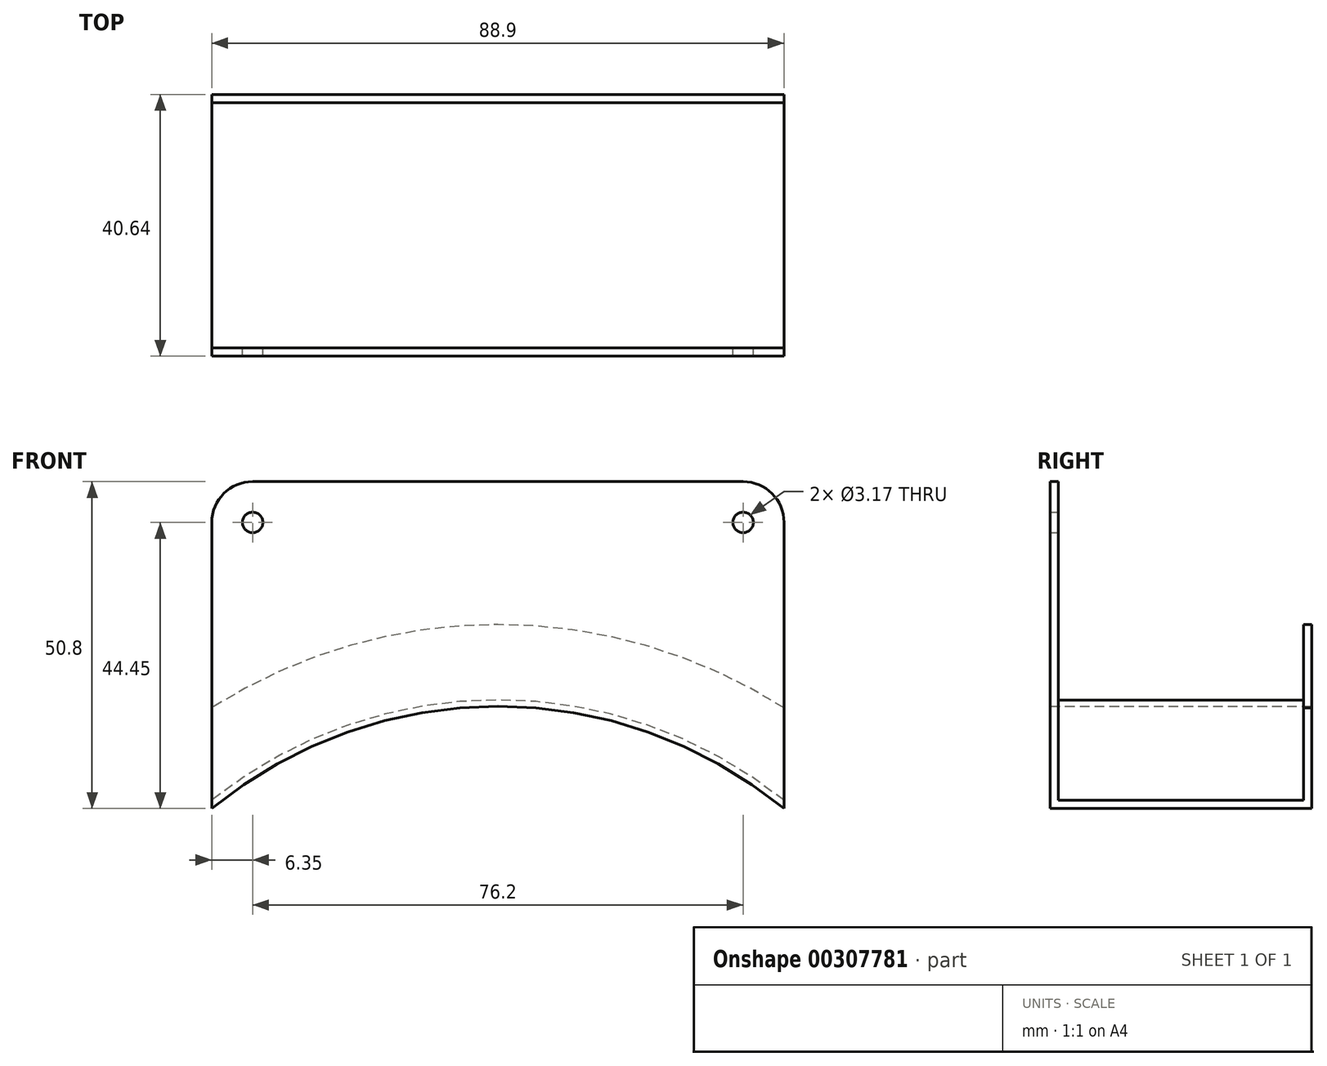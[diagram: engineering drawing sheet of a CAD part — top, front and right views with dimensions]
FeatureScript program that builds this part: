
annotation { "Feature Type Name" : "Feature", "Feature Type Description" : "" }
export const myFeature = defineFeature(function(context is Context, id is Id, definition is map)
    precondition{}
    {
        {
            var Q0;
            Q0=qCreatedBy(makeId("Front.planeOp"),FACE);
            var sketch = newSketch(context, id + "F0", { "sketchPlane" : qUnion([Q0])});
            skLineSegment(sketch, "E0", {"start": v(-44.45, 0) * mm, "end": v(44.45, 0) * mm});
            skArc(sketch, "E1", {"start": v(44.45, 0) * mm, "mid": v(0, 15.88) * mm, "end": v(-44.45, 0) * mm});
            skPoint(sketch, "E2", {"position": v(0, 15.88) * mm});
            skPoint(sketch, "E3", {"position": v(0, 28.58) * mm});
            skArc(sketch, "E4", {"start": v(44.45, 15.64) * mm, "mid": v(0, 28.58) * mm, "end": v(-44.45, 15.64) * mm});
            skLineSegment(sketch, "E5", {"start": v(-44.45, 15.64) * mm, "end": v(-44.45, 0) * mm});
            skLineSegment(sketch, "E6", {"start": v(44.45, 15.64) * mm, "end": v(44.45, 0) * mm});
            skSolve(sketch);
        }
        {
            var Q0;
            Q0=makeQuery(id+"F0.imprint","IMPRINT",FACE,{"disambiguationData":[TD([[makeQuery(id+"F0.imprint","IMPRINT",EDGE,{"derivedFrom":sQuery(id+"F0.wireOp",EDGE,"E1")}),-1.0]])]});
            extrude(context, id + "F1", {"entities" : qUnion([Q0]), "depth" : 1.27 * mm});
        }
        {
            var Q0;
            Q0=makeQuery(id+"F1.opExtrude","CAP_FACE",FACE,{"disambiguationData":[OSD([sQuery(id+"F0.wireOp",EDGE,"E1"),sQuery(id+"F0.wireOp",EDGE,"E4"),sQuery(id+"F0.wireOp",EDGE,"E5"),sQuery(id+"F0.wireOp",EDGE,"E6")])],"isStart":false});
            var sketch = newSketch(context, id + "F2", { "sketchPlane" : qUnion([Q0])});
            skArc(sketch, "E7", {"start": v(44.45, 0) * mm, "mid": v(0, 15.88) * mm, "end": v(-44.45, 0) * mm});
            skArc(sketch, "E8", {"start": v(44.45, 1.27) * mm, "mid": v(0, 16.86) * mm, "end": v(-44.45, 1.27) * mm});
            skLineSegment(sketch, "E9", {"start": v(44.45, 1.27) * mm, "end": v(44.45, 0) * mm});
            skSolve(sketch);
        }
        {
            var Q0;
            {var subQ0=sQuery(id+"F2.wireOp",EDGE,"E7");Q0=makeQuery(id+"F2.imprint","IMPRINT",FACE,{"disambiguationData":[TD([[makeQuery(id+"F2.imprint","IMPRINT",EDGE,{"derivedFrom":subQ0}),-1.0]])]});}
            extrude(context, id + "F3", {"entities" : qUnion([Q0]), "operationType" : NewBodyOperationType.ADD, "depth" : 38.1 * mm});
        }
        {
            var Q0;
            Q0=makeQuery(id+"F3.opExtrude","CAP_FACE",FACE,{"disambiguationData":[OSD([sQuery(id+"F0.wireOp",EDGE,"E5"),sQuery(id+"F2.wireOp",EDGE,"E7"),sQuery(id+"F2.wireOp",EDGE,"E8"),sQuery(id+"F2.wireOp",EDGE,"E9")])],"isStart":false});
            var sketch = newSketch(context, id + "F4", { "sketchPlane" : qUnion([Q0])});
            skLineSegment(sketch, "E10", {"start": v(-44.45, 0) * mm, "end": v(-44.45, 44.45) * mm});
            skLineSegment(sketch, "E11", {"start": v(44.45, 0) * mm, "end": v(44.45, 44.45) * mm});
            skPoint(sketch, "E11.endSnap0", {"position": v(44.45, 0.64) * mm});
            skLineSegment(sketch, "E12", {"start": v(-38.1, 50.8) * mm, "end": v(38.1, 50.8) * mm});
            skPoint(sketch, "E13.visualSharp", {"position": v(-44.45, 50.8) * mm});
            skArc(sketch, "E13.filletArc", {"start": v(-38.1, 50.8) * mm, "mid": v(-42.6, 48.94) * mm, "end": v(-44.45, 44.45) * mm});
            skPoint(sketch, "E14.visualSharp", {"position": v(44.45, 50.8) * mm});
            skArc(sketch, "E14.filletArc", {"start": v(44.45, 44.45) * mm, "mid": v(42.6, 48.94) * mm, "end": v(38.1, 50.8) * mm});
            skArc(sketch, "E15", {"start": v(44.45, 0) * mm, "mid": v(0, 15.88) * mm, "end": v(-44.45, 0) * mm});
            skSolve(sketch);
        }
        {
            var Q0;
            Q0 = qSketchRegion(id + "F4", true);
            extrude(context, id + "F5", {"entities" : qUnion([Q0]), "operationType" : NewBodyOperationType.ADD, "depth" : 1.27 * mm});
        }
        {
            var Q0;
            Q0=makeQuery(id+"F5.opExtrude","CAP_FACE",FACE,{"disambiguationData":[OSD([sQuery(id+"F4.wireOp",EDGE,"E10"),sQuery(id+"F4.wireOp",EDGE,"E11"),sQuery(id+"F4.wireOp",EDGE,"E12"),sQuery(id+"F4.wireOp",EDGE,"E13.filletArc"),sQuery(id+"F4.wireOp",EDGE,"E14.filletArc"),sQuery(id+"F4.wireOp",EDGE,"E15")])],"isStart":true});
            var sketch = newSketch(context, id + "F6", { "sketchPlane" : qUnion([Q0])});
            skCircle(sketch, "E16", {"center": v(-38.1, 44.45) * mm, "radius": 1.59 * mm});
            skCircle(sketch, "E17", {"center": v(38.1, 44.45) * mm, "radius": 1.59 * mm});
            skSolve(sketch);
        }
        {
            var Q0;
            Q0=makeQuery(id+"F6.imprint","IMPRINT",FACE,{"disambiguationData":[TD([[makeQuery(id+"F6.imprint","IMPRINT",EDGE,{"derivedFrom":sQuery(id+"F6.wireOp",EDGE,"E16")}),1.0]])]});
            var Q1;
            Q1=makeQuery(id+"F6.imprint","IMPRINT",FACE,{"disambiguationData":[TD([[makeQuery(id+"F6.imprint","IMPRINT",EDGE,{"derivedFrom":sQuery(id+"F6.wireOp",EDGE,"E17")}),1.0]])]});
            extrude(context, id + "F7", {"entities" : qUnion([Q0, Q1]), "operationType" : NewBodyOperationType.REMOVE, "oppositeDirection" : true, "depth" : 25.4 * mm});
        }
    });
